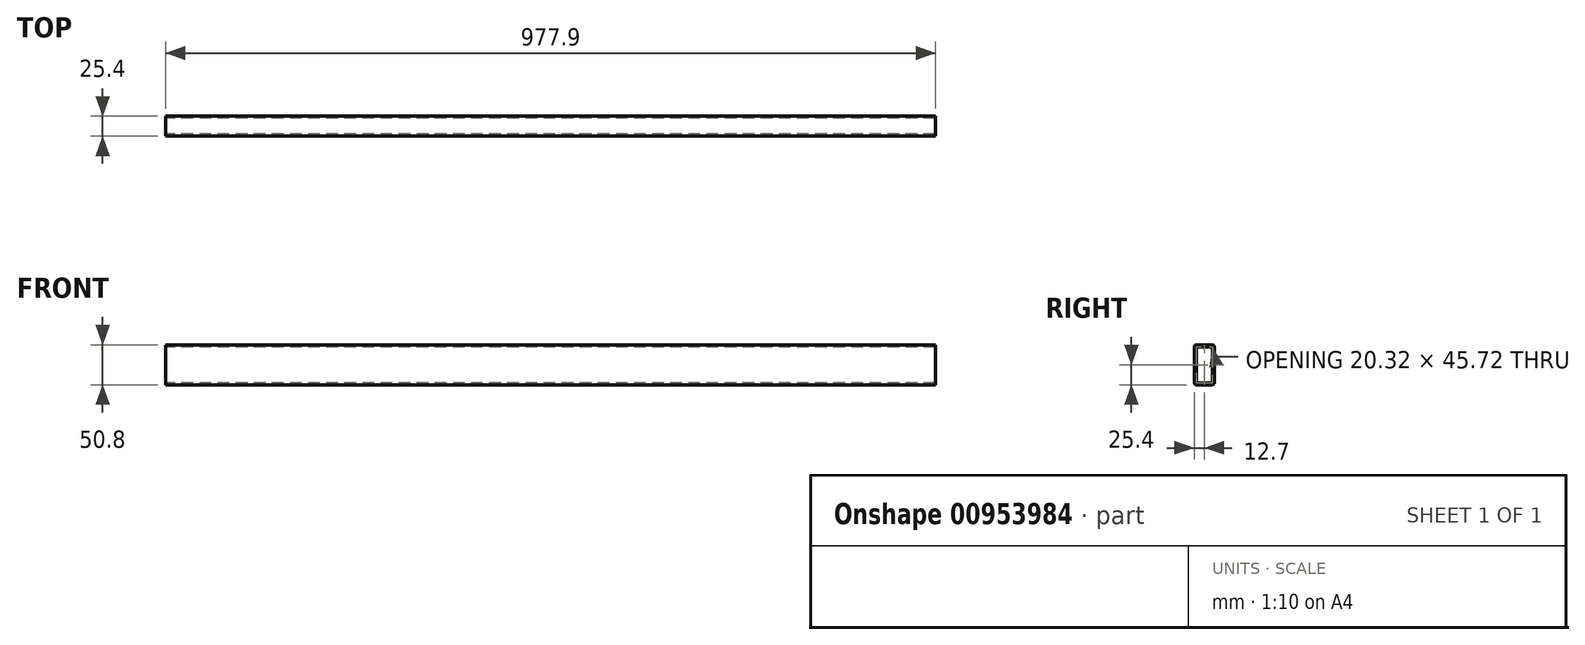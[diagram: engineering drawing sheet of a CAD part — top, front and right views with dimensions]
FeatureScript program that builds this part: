
annotation { "Feature Type Name" : "Feature", "Feature Type Description" : "" }
export const myFeature = defineFeature(function(context is Context, id is Id, definition is map)
    precondition{}
    {
        {
            var Q0;
            Q0=qCreatedBy(makeId("Front.planeOp"),FACE);
            var sketch = newSketch(context, id + "F0", { "sketchPlane" : qUnion([Q0])});
            skLineSegment(sketch, "E0.bottom", {"start": v(488.95, -25.4) * mm, "end": v(-488.95, -25.4) * mm});
            skLineSegment(sketch, "E0.top", {"start": v(488.95, 25.4) * mm, "end": v(-488.95, 25.4) * mm});
            skLineSegment(sketch, "E0.left", {"start": v(488.95, -25.4) * mm, "end": v(488.95, 25.4) * mm});
            skLineSegment(sketch, "E0.right", {"start": v(-488.95, -25.4) * mm, "end": v(-488.95, 25.4) * mm});
            skPoint(sketch, "E0.middle", {"position": v(0, 0) * mm});
            skSolve(sketch);
        }
        {
            var Q0;
            Q0=makeQuery(id+"F0.imprint","IMPRINT",FACE,{"disambiguationData":[TD([[makeQuery(id+"F0.imprint","IMPRINT",EDGE,{"derivedFrom":sQuery(id+"F0.wireOp",EDGE,"E0.bottom")}),-1.0]])]});
            extrude(context, id + "F1", {"entities" : qUnion([Q0]), "endBound" : BoundingType.SYMMETRIC, "depth" : 25.4 * mm, "offsetDistance" : 25.4 * mm});
        }
        {
            var Q0;
            Q0=makeQuery(id+"F1.opExtrude","SWEPT_FACE",FACE,{"disambiguationData":[OSD([sQuery(id+"F0.wireOp",EDGE,"E0.right")])]});
            var Q1;
            Q1=makeQuery(id+"F1.opExtrude","SWEPT_FACE",FACE,{"disambiguationData":[OSD([sQuery(id+"F0.wireOp",EDGE,"E0.left")])]});
            shell(context, id + "F2", {"entities" : qUnion([Q0, Q1]), "thickness" : 2.54 * mm});
        }
        {
            var Q0;
            Q0=makeQuery(id+"F1.opExtrude","CAP_EDGE",EDGE,{"disambiguationData":[OSD([sQuery(id+"F0.wireOp",EDGE,"E0.top")])],"isStart":false});
            var Q1;
            Q1=makeQuery(id+"F1.opExtrude","CAP_EDGE",EDGE,{"disambiguationData":[OSD([sQuery(id+"F0.wireOp",EDGE,"E0.top")])],"isStart":true});
            var Q2;
            Q2=makeQuery(id+"F1.opExtrude","CAP_EDGE",EDGE,{"disambiguationData":[OSD([sQuery(id+"F0.wireOp",EDGE,"E0.bottom")])],"isStart":true});
            var Q3;
            Q3=makeQuery(id+"F1.opExtrude","CAP_EDGE",EDGE,{"disambiguationData":[OSD([sQuery(id+"F0.wireOp",EDGE,"E0.bottom")])],"isStart":false});
            fillet(context, id + "F3", {"entities" : qUnion([Q0, Q1, Q2, Q3]), "radius" : 2.54 * mm, "tangentPropagation" : true, "allowEdgeOverflow" : false});
        }
        {
            var Q0;
            {var subQ0=sQuery(id+"F0.wireOp",EDGE,"E0.top");Q0=makeQuery(id+"F2.opShell","OFFSET_EDGE",EDGE,{"disambiguationData":[OSD([subQ0]),TDD([makeQuery(id+"F1.opExtrude","CAP_EDGE",EDGE,{"disambiguationData":[OSD([subQ0])],"isStart":false})])]});}
            var Q1;
            {var subQ0=sQuery(id+"F0.wireOp",EDGE,"E0.top");Q1=makeQuery(id+"F2.opShell","OFFSET_EDGE",EDGE,{"disambiguationData":[OSD([subQ0]),TDD([makeQuery(id+"F1.opExtrude","CAP_EDGE",EDGE,{"disambiguationData":[OSD([subQ0])],"isStart":true})])]});}
            var Q2;
            {var subQ0=sQuery(id+"F0.wireOp",EDGE,"E0.bottom");Q2=makeQuery(id+"F2.opShell","OFFSET_EDGE",EDGE,{"disambiguationData":[OSD([subQ0]),TDD([makeQuery(id+"F1.opExtrude","CAP_EDGE",EDGE,{"disambiguationData":[OSD([subQ0])],"isStart":true})])]});}
            var Q3;
            {var subQ0=sQuery(id+"F0.wireOp",EDGE,"E0.bottom");Q3=makeQuery(id+"F2.opShell","OFFSET_EDGE",EDGE,{"disambiguationData":[OSD([subQ0]),TDD([makeQuery(id+"F1.opExtrude","CAP_EDGE",EDGE,{"disambiguationData":[OSD([subQ0])],"isStart":false})])]});}
            fillet(context, id + "F4", {"entities" : qUnion([Q0, Q1, Q2, Q3]), "radius" : 1.27 * mm, "tangentPropagation" : true, "allowEdgeOverflow" : false});
        }
    });
